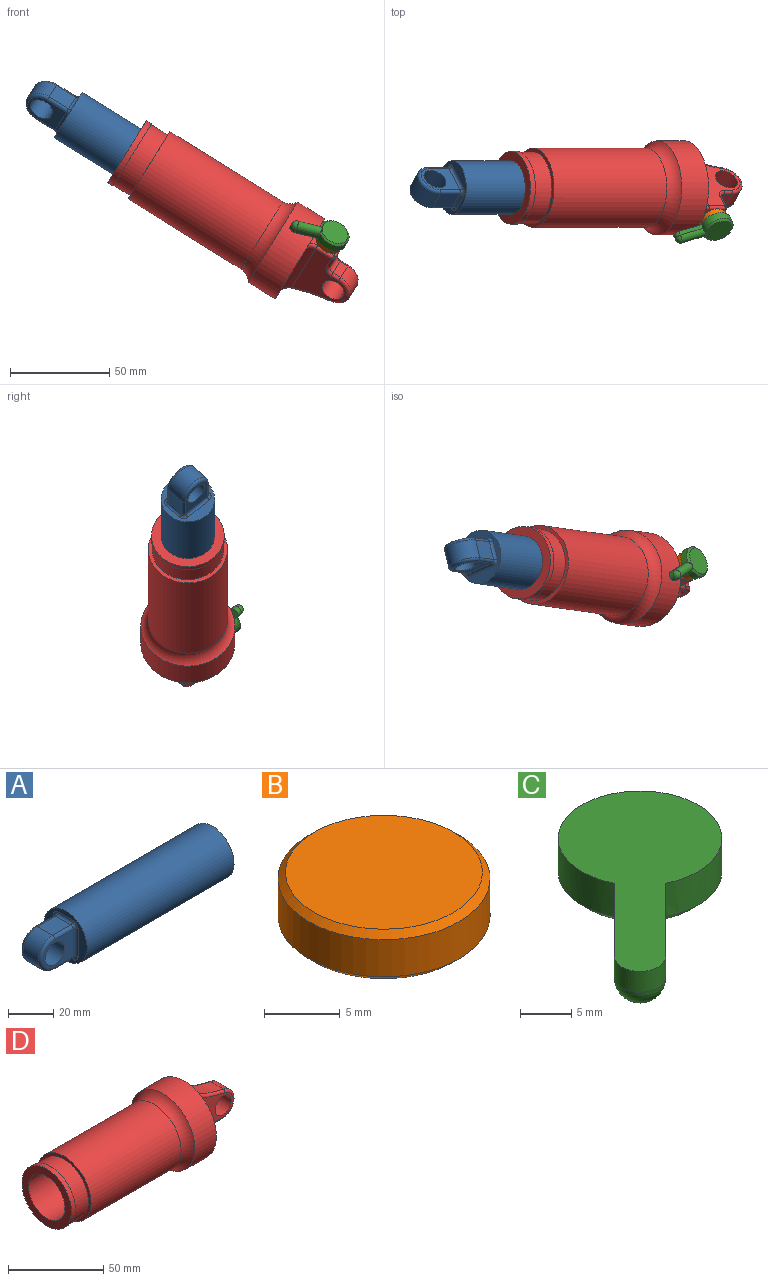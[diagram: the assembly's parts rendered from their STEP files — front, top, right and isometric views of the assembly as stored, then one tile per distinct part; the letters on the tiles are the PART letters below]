
ASSEMBLY  parts=4 mates=3
PART A: 23 faces, bbox 114.7x27x27 mm
  f0: plane 27x27mm, normal (-1,0,0), area 254.8mm2, adj f1,f14,f15,f16,f17,f18,f19,f20
  f1: cylinder r=13.5mm len=92mm, axis (-1,0,0), area 7803.7mm2, adj f0,f2
  f2: plane 27x27mm, normal (1,0,0), area 572.6mm2, adj f1
  f3: plane 11.5x9.5mm, normal (0,0,1), area 109.2mm2, adj f4,f8,f11,f14
  f4: cylinder r=9mm len=18mm, axis (0,1,0), area 268.6mm2, adj f3,f5,f9,f12
  f5: plane 11.5x9.5mm, normal (0,0,-1), area 109.2mm2, adj f4,f10,f13,f21
  f6: plane 19x15mm, normal (0,-1,0), area 147.8mm2, adj f11,f12,f13,f17,f22
  f7: plane 19x15mm, normal (0,1,0), area 147.8mm2, adj f8,f9,f10,f18,f22
  f8: cylinder r=1.5mm len=11.5mm, axis (-1,0,0), area 27.1mm2, adj f3,f7,f9,f16
  f9: torus R=7.5mm, axis (0,-1,0), area 62.6mm2, adj f4,f7,f8,f10
  f10: cylinder r=1.5mm len=11.5mm, axis (1,0,0), area 27.1mm2, adj f5,f7,f9,f20
  f11: cylinder r=1.5mm len=11.5mm, axis (1,0,0), area 27.1mm2, adj f3,f6,f12,f15
  f12: torus R=7.5mm, axis (0,-1,0), area 62.6mm2, adj f4,f6,f11,f13
  f13: cylinder r=1.5mm len=11.5mm, axis (-1,0,0), area 27.1mm2, adj f5,f6,f12,f19
  f14: cylinder r=1.5mm len=9.5mm, axis (0,-1,0), area 22.4mm2, adj f0,f3,f15,f16
  f15: torus R=3mm, axis (-1,0,0), area 7.6mm2, adj f0,f11,f14,f17
  f16: torus R=3mm, axis (-1,0,0), area 7.6mm2, adj f0,f8,f14,f18
  f17: cylinder r=1.5mm len=15mm, axis (0,0,-1), area 35.3mm2, adj f0,f6,f15,f19
  f18: cylinder r=1.5mm len=15mm, axis (0,0,1), area 35.3mm2, adj f0,f7,f16,f20
  f19: torus R=3mm, axis (-1,0,0), area 7.6mm2, adj f0,f13,f17,f21
  f20: torus R=3mm, axis (-1,0,0), area 7.6mm2, adj f0,f10,f18,f21
  f21: cylinder r=1.5mm len=9.5mm, axis (0,1,0), area 22.4mm2, adj f0,f5,f19,f20
  f22: cylinder r=6mm len=12.5mm, axis (0,-1,0), area 471.2mm2, adj f6,f7
PART B: 5 faces, bbox 14x14x4 mm
  f0: cylinder r=7mm len=14mm, axis (0,0,1), area 131.9mm2, adj f3,f4
  f1: plane 13x13mm, normal (0,0,-1), area 132.7mm2, adj f4
  f2: plane 13x13mm, normal (0,0,1), area 132.7mm2, adj f3
  f3: cone r=7mm half-angle=45deg, axis (0,0,-1), area 30mm2, adj f0,f2
  f4: cone r=6.5mm half-angle=45deg, axis (0,0,1), area 30mm2, adj f0,f1
PART C: 9 faces, bbox 24.6x24.6x5 mm
  f0: cylinder r=2.5mm len=4.27mm, axis (0,0,1), area 19.6mm2, adj f1,f3,f5,f7
  f1: plane 8.77x8.77mm, normal (-0.71,0.71,0), area 31mm2, adj f0,f2,f5,f8
  f2: cylinder r=8mm len=16mm, axis (0,0,1), area 181.2mm2, adj f1,f3,f5,f6,f8
  f3: plane 8.77x8.77mm, normal (0.71,-0.71,0), area 31mm2, adj f0,f2,f5,f8
  f4: plane 14x14mm, normal (0,0,-1), area 153.9mm2, adj f6
  f5: plane 24.64x24.64mm, normal (0,0,1), area 271.5mm2, adj f0,f1,f2,f3
  f6: cone r=7mm half-angle=45deg, axis (0,0,1), area 62.7mm2, adj f2,f4,f8
  f7: sphere r=2.5mm, area 19.6mm2, adj f0,f8
  f8: cylinder r=2.5mm len=12.73mm, axis (0.71,0.71,0), area 98.9mm2, adj f1,f2,f3,f6,f7
PART D: 43 faces, bbox 135.2x60x60 mm
  f0: plane 9.5x4.5mm, normal (0,0,-1), area 42.8mm2, adj f12,f22,f27,f36
  f1: plane 47.93x47.93mm, normal (1,0,0), area 998.8mm2, adj f5,f13,f17,f18,f19,f24,f32,f33
  f2: plane 36.8x36.8mm, normal (-1,0,0), area 491.1mm2, adj f3,f11
  f3: cylinder r=13.5mm len=86.5mm, axis (-1,0,0), area 7337.2mm2, adj f2,f4
  f4: plane 27x27mm, normal (-1,0,0), area 572.6mm2, adj f3
  f5: cylinder r=23.75mm len=47.5mm, axis (-1,0,0), area 2387.6mm2, adj f1,f6
  f6: torus R=27.51mm, axis (-1,0,0), area 1051.5mm2, adj f5,f7
  f7: cylinder r=20mm len=67mm, axis (-1,0,0), area 8419.5mm2, adj f6,f8
  f8: plane 40x40mm, normal (-1,0,0), area 238.8mm2, adj f7,f9
  f9: cylinder r=18mm len=36mm, axis (-1,0,0), area 1131mm2, adj f8,f10
  f10: plane 36.8x36.8mm, normal (1,0,0), area 45.7mm2, adj f9,f11
  f11: cylinder r=18.4mm len=36.8mm, axis (-1,0,0), area 346.8mm2, adj f2,f10
  f12: cylinder r=9mm len=17.84mm, axis (0,1,0), area 252.5mm2, adj f0,f13,f26,f35
  f13: cylinder r=75mm len=24.19mm, axis (0,1,0), area 261.6mm2, adj f1,f12,f24,f25,f33,f34
  f14: plane 32.61x26mm, normal (0,-1,0), area 415.9mm2, adj f19,f25,f26,f27,f28,f29,f31,f42
  f15: plane 32.61x26mm, normal (0,1,0), area 415.9mm2, adj f18,f34,f35,f36,f37,f38,f40,f42
  f16: plane 9.5x7mm, normal (1,0,0), area 66.5mm2, adj f22,f23,f29,f38
  f17: plane 14x12.95mm, normal (0,0,-1), area 87mm2, adj f1,f20,f23,f31,f32,f40,f41
  f18: cylinder r=4mm len=35.65mm, axis (0,0,-1), area 214.4mm2, adj f1,f15,f33,f41
  f19: cylinder r=4mm len=35.65mm, axis (0,0,1), area 214.4mm2, adj f1,f14,f24,f32
  f20: cylinder r=4mm len=8mm, axis (0,0,1), area 25.1mm2, adj f17,f21
  f21: plane 8x8mm, normal (0,0,-1), area 50.3mm2, adj f20
  f22: cylinder r=3mm len=9.5mm, axis (0,-1,0), area 44.8mm2, adj f0,f16,f28,f37
  f23: cylinder r=1mm len=9.5mm, axis (0,1,0), area 14.9mm2, adj f16,f17,f30,f39
  f24: bspline ~6.69x6.15mm, area 12.8mm2, adj f1,f13,f19,f25
  f25: torus R=76.5mm, axis (0,-1,0), area 49.1mm2, adj f13,f14,f24,f26
  f26: torus R=7.5mm, axis (0,-1,0), area 58.8mm2, adj f12,f14,f25,f27
  f27: cylinder r=1.5mm len=4.5mm, axis (-1,0,0), area 10.6mm2, adj f0,f14,f26,f28
  f28: torus R=4.5mm, axis (0,-1,0), area 13.1mm2, adj f14,f22,f27,f29
  f29: cylinder r=1.5mm len=7mm, axis (0,0,1), area 15.9mm2, adj f14,f16,f28,f30
  f30: bspline ~1.58x1.5mm, area 1.6mm2, adj f23,f29,f31
  f31: cylinder r=1.5mm len=10mm, axis (-1,0,0), area 23mm2, adj f14,f17,f30,f32
  f32: torus R=5.5mm, axis (0,0,-1), area 12.5mm2, adj f1,f17,f19,f31
  f33: bspline ~6.69x6.15mm, area 12.8mm2, adj f1,f13,f18,f34
  f34: torus R=76.5mm, axis (0,-1,0), area 49.1mm2, adj f13,f15,f33,f35
  f35: torus R=7.5mm, axis (0,-1,0), area 58.8mm2, adj f12,f15,f34,f36
  f36: cylinder r=1.5mm len=4.5mm, axis (1,0,0), area 10.6mm2, adj f0,f15,f35,f37
  f37: torus R=4.5mm, axis (0,-1,0), area 13.1mm2, adj f15,f22,f36,f38
  f38: cylinder r=1.5mm len=7mm, axis (0,0,-1), area 15.9mm2, adj f15,f16,f37,f39
  f39: bspline ~1.58x1.5mm, area 1.6mm2, adj f23,f38,f40
  f40: cylinder r=1.5mm len=10mm, axis (1,0,0), area 23mm2, adj f15,f17,f39,f41
  f41: torus R=5.5mm, axis (0,0,-1), area 12.5mm2, adj f1,f17,f18,f40
  f42: cylinder r=6mm len=12.5mm, axis (0,-1,0), area 471.2mm2, adj f14,f15
PLACE A rot(axis=(-0.96,0.12,0.27),135.8deg) t=(-14.69,4.62,4.02)mm
PLACE B rot(axis=(-0.96,0.12,0.27),135.8deg) t=(-37.63,4.62,18.25)mm
PLACE C rot(axis=(-0.89,-0.46,-0.01),126.1deg) t=(-2.6,-115.41,-150.05)mm
PLACE D rot(axis=(-0.96,0.12,0.27),135.8deg) t=(-37.63,4.62,18.25)mm fixed
MATE revolute C.f6 <-> B.f0  axis (-0.37,0.72,-0.59) through (129.14,-13.38,-64.8)mm
MATE fastened B.f3 <-> D.f20  axis (-0.37,0.72,-0.59) through (127.68,-10.5,-67.15)mm
MATE slider D.f3 <-> A.f1  axis (-0.85,0,0.53) through (26.1,4.62,-21.29)mm
